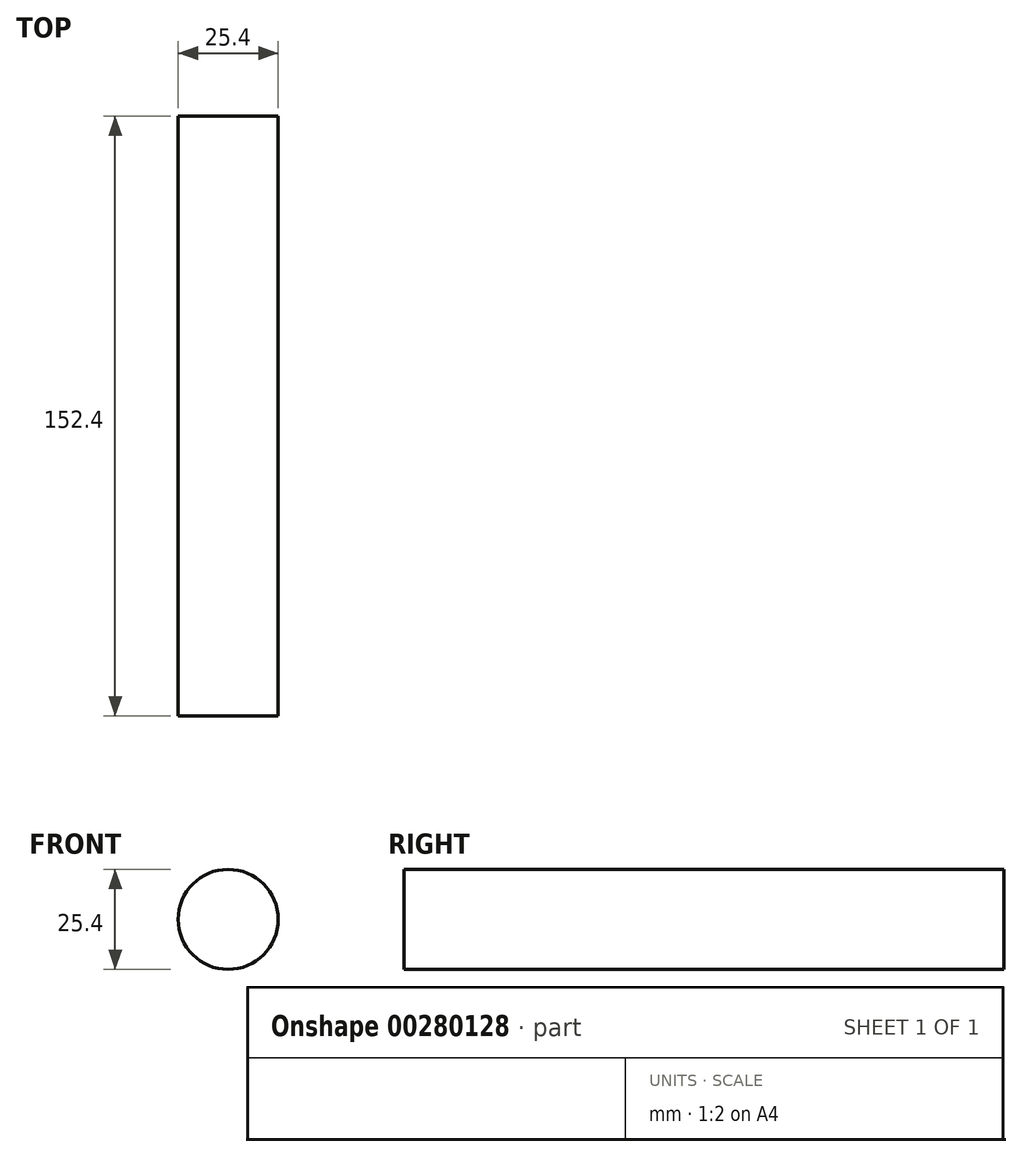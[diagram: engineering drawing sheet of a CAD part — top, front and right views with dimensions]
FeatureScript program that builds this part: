
annotation { "Feature Type Name" : "Feature", "Feature Type Description" : "" }
export const myFeature = defineFeature(function(context is Context, id is Id, definition is map)
    precondition{}
    {
        {
            var Q0;
            Q0=qCreatedBy(makeId("Front.planeOp"),FACE);
            var sketch = newSketch(context, id + "F0", { "sketchPlane" : qUnion([Q0])});
            skCircle(sketch, "E0", {"center": v(-32.57, 33.68) * mm, "radius": 12.7 * mm});
            skSolve(sketch);
        }
        {
            var Q0;
            Q0 = qSketchRegion(id + "F0", true);
            extrude(context, id + "F1", {"entities" : qUnion([Q0]), "depth" : 152.4 * mm});
        }
    });
